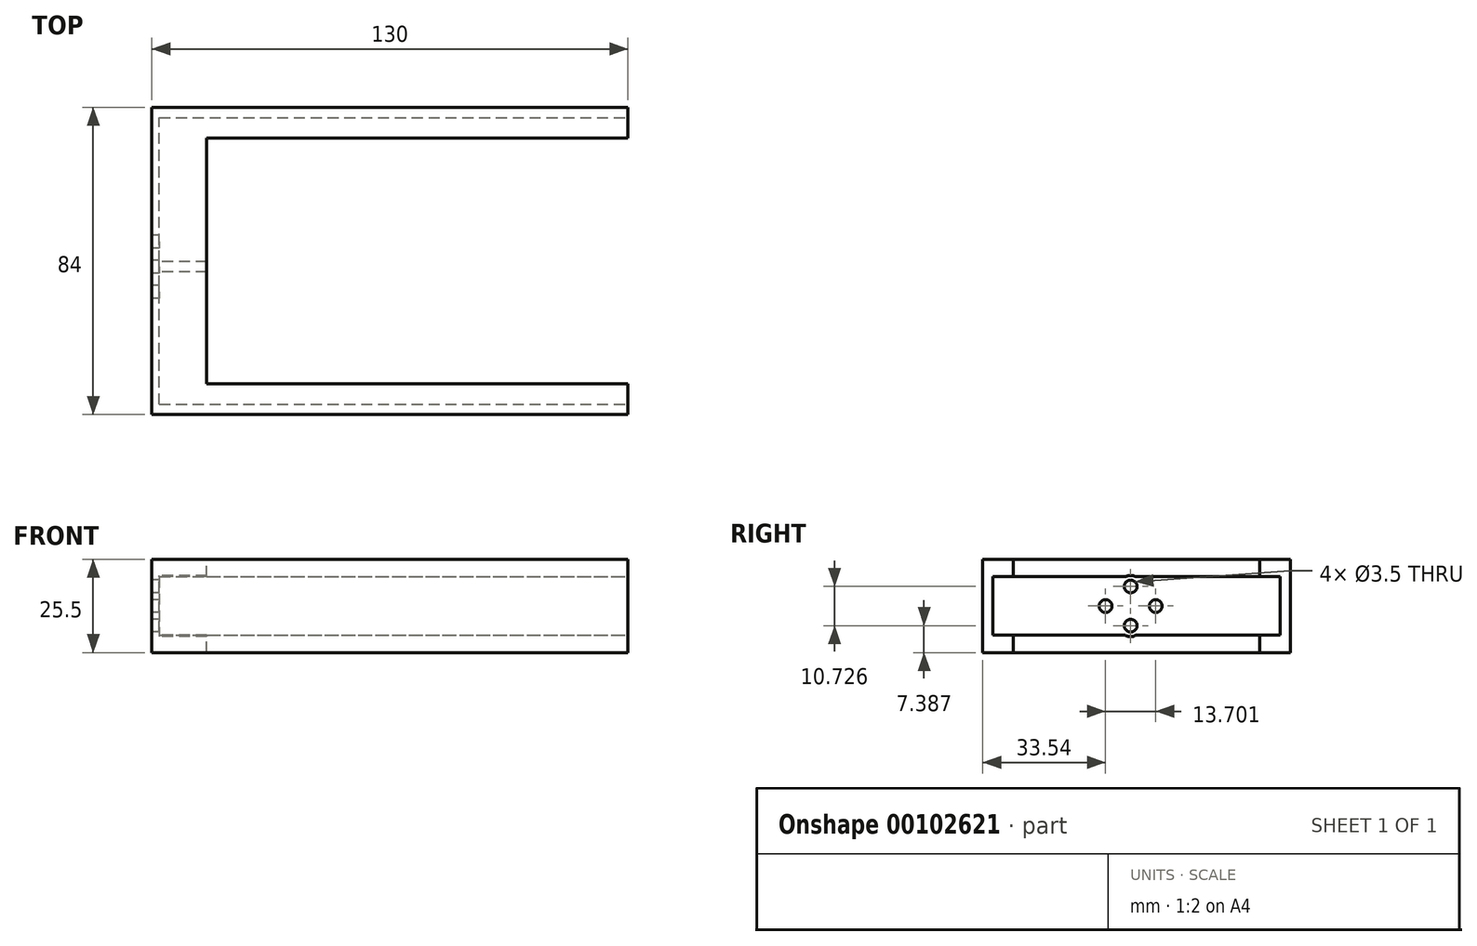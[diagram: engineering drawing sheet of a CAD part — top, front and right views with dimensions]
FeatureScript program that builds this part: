
annotation { "Feature Type Name" : "Feature", "Feature Type Description" : "" }
export const myFeature = defineFeature(function(context is Context, id is Id, definition is map)
    precondition{}
    {
        {
            var Q0;
            Q0=qCreatedBy(makeId("Top.planeOp"),FACE);
            var sketch = newSketch(context, id + "F0", { "sketchPlane" : qUnion([Q0])});
            skLineSegment(sketch, "E0.bottom", {"start": v(-85.3, 43.6) * mm, "end": v(44.7, 43.6) * mm});
            skLineSegment(sketch, "E0.top", {"start": v(-85.3, -40.4) * mm, "end": v(44.7, -40.4) * mm});
            skLineSegment(sketch, "E0.left", {"start": v(-85.3, 43.6) * mm, "end": v(-85.3, -40.4) * mm});
            skLineSegment(sketch, "E0.right", {"start": v(44.7, 43.6) * mm, "end": v(44.7, -40.4) * mm});
            skSolve(sketch);
        }
        {
            var Q0;
            Q0 = qSketchRegion(id + "F0", true);
            extrude(context, id + "F1", {"entities" : qUnion([Q0]), "depth" : 25.5 * mm});
        }
        {
            var Q0;
            Q0=makeQuery(id+"F1.opExtrude","SWEPT_FACE",FACE,{"disambiguationData":[OSD([sQuery(id+"F0.wireOp",EDGE,"E0.right")])]});
            var sketch = newSketch(context, id + "F2", { "sketchPlane" : qUnion([Q0])});
            skLineSegment(sketch, "E1.bottom", {"start": v(-37.6, 20.75) * mm, "end": v(40.8, 20.75) * mm});
            skLineSegment(sketch, "E1.top", {"start": v(-37.6, 4.75) * mm, "end": v(40.8, 4.75) * mm});
            skLineSegment(sketch, "E1.left", {"start": v(-37.6, 20.75) * mm, "end": v(-37.6, 4.75) * mm});
            skLineSegment(sketch, "E1.right", {"start": v(40.8, 20.75) * mm, "end": v(40.8, 4.75) * mm});
            skSolve(sketch);
        }
        {
            var Q0;
            Q0 = qSketchRegion(id + "F2", true);
            extrude(context, id + "F3", {"entities" : qUnion([Q0]), "operationType" : NewBodyOperationType.REMOVE, "oppositeDirection" : true, "depth" : 128 * mm});
        }
        {
            var Q0;
            Q0=makeQuery(id+"F1.opExtrude","CAP_FACE",FACE,{"disambiguationData":[OSD([sQuery(id+"F0.wireOp",EDGE,"E0.bottom"),sQuery(id+"F0.wireOp",EDGE,"E0.top"),sQuery(id+"F0.wireOp",EDGE,"E0.left"),sQuery(id+"F0.wireOp",EDGE,"E0.right")])],"isStart":false});
            var sketch = newSketch(context, id + "F4", { "sketchPlane" : qUnion([Q0])});
            skLineSegment(sketch, "E2.bottom", {"start": v(44.7, 35.24) * mm, "end": v(-70.3, 35.24) * mm});
            skLineSegment(sketch, "E2.top", {"start": v(44.7, -32.02) * mm, "end": v(-70.3, -32.02) * mm});
            skLineSegment(sketch, "E2.left", {"start": v(44.7, 35.24) * mm, "end": v(44.7, -32.02) * mm});
            skLineSegment(sketch, "E2.right", {"start": v(-70.3, 35.24) * mm, "end": v(-70.3, -32.02) * mm});
            skSolve(sketch);
        }
        {
            var Q0;
            Q0 = qSketchRegion(id + "F4", true);
            extrude(context, id + "F5", {"entities" : qUnion([Q0]), "operationType" : NewBodyOperationType.REMOVE, "endBound" : BoundingType.THROUGH_ALL, "oppositeDirection" : true, "depth" : 25 * mm});
        }
        {
            var Q0;
            Q0=makeQuery(id+"F1.opExtrude","SWEPT_FACE",FACE,{"disambiguationData":[OSD([sQuery(id+"F0.wireOp",EDGE,"E0.left")])]});
            var sketch = newSketch(context, id + "F6", { "sketchPlane" : qUnion([Q0])});
            skLineSegment(sketch, "E3", {"start": v(0, 35.16) * mm, "end": v(0, -14.82) * mm, "construction": true});
            skLineSegment(sketch, "E4", {"start": v(40.4, 12.75) * mm, "end": v(-46.69, 12.75) * mm, "construction": true});
            skCircle(sketch, "E5", {"center": v(0, 18.11) * mm, "radius": 1.75 * mm});
            skCircle(sketch, "E6", {"center": v(0, 7.39) * mm, "radius": 1.75 * mm});
            skCircle(sketch, "E7", {"center": v(-6.85, 12.75) * mm, "radius": 1.75 * mm});
            skCircle(sketch, "E8", {"center": v(6.85, 12.75) * mm, "radius": 1.75 * mm});
            skSolve(sketch);
        }
        {
            var Q0;
            Q0 = qSketchRegion(id + "F6", true);
            extrude(context, id + "F7", {"entities" : qUnion([Q0]), "operationType" : NewBodyOperationType.REMOVE, "endBound" : BoundingType.THROUGH_ALL, "oppositeDirection" : true, "depth" : 25 * mm});
        }
        {
            var Q0;
            Q0=makeQuery(id+"F3.boolean.opBoolean","COPY",FACE,{"derivedFrom":makeQuery(id+"F3.opExtrude","CAP_FACE",FACE,{"disambiguationData":[OSD([sQuery(id+"F2.wireOp",EDGE,"E1.bottom"),sQuery(id+"F2.wireOp",EDGE,"E1.top"),sQuery(id+"F2.wireOp",EDGE,"E1.left"),sQuery(id+"F2.wireOp",EDGE,"E1.right")])],"isStart":false})});
            var sketch = newSketch(context, id + "F8", { "sketchPlane" : qUnion([Q0])});
            skSolve(sketch);
        }
        {
            var Q0;
            {var subQ3=sQuery(id+"F2.wireOp",EDGE,"E1.bottom");Q0=makeQuery(id+"F8.imprint","IMPRINT",FACE,{"disambiguationData":[TD([[makeQuery(id+"F8.imprint","IMPRINT",EDGE,{"derivedFrom":makeQuery(id+"F3.boolean.opBoolean","COPY",EDGE,{"derivedFrom":makeQuery(id+"F3.opExtrude","CAP_EDGE",EDGE,{"disambiguationData":[OSD([subQ3])],"isStart":false})})}),-1.0]])]});}
            var sketch = newSketch(context, id + "F9", { "sketchPlane" : qUnion([Q0])});
            skCircle(sketch, "E9", {"center": v(0, 18.11) * mm, "radius": 3 * mm});
            skSolve(sketch);
        }
        {
            var Q0;
            Q0 = qSketchRegion(id + "F9", true);
            extrude(context, id + "F10", {"entities" : qUnion([Q0]), "operationType" : NewBodyOperationType.REMOVE, "depth" : 25 * mm});
        }
        {
            var Q0;
            {var subQ3=sQuery(id+"F2.wireOp",EDGE,"E1.bottom");Q0=makeQuery(id+"F8.imprint","IMPRINT",FACE,{"disambiguationData":[TD([[makeQuery(id+"F8.imprint","IMPRINT",EDGE,{"derivedFrom":makeQuery(id+"F3.boolean.opBoolean","COPY",EDGE,{"derivedFrom":makeQuery(id+"F3.opExtrude","CAP_EDGE",EDGE,{"disambiguationData":[OSD([subQ3])],"isStart":false})})}),-1.0]])]});}
            var sketch = newSketch(context, id + "F11", { "sketchPlane" : qUnion([Q0])});
            skCircle(sketch, "E10", {"center": v(0, 7.39) * mm, "radius": 3 * mm});
            skSolve(sketch);
        }
        {
            var Q0;
            Q0 = qSketchRegion(id + "F11", true);
            extrude(context, id + "F12", {"entities" : qUnion([Q0]), "operationType" : NewBodyOperationType.REMOVE, "depth" : 25 * mm});
        }
    });
